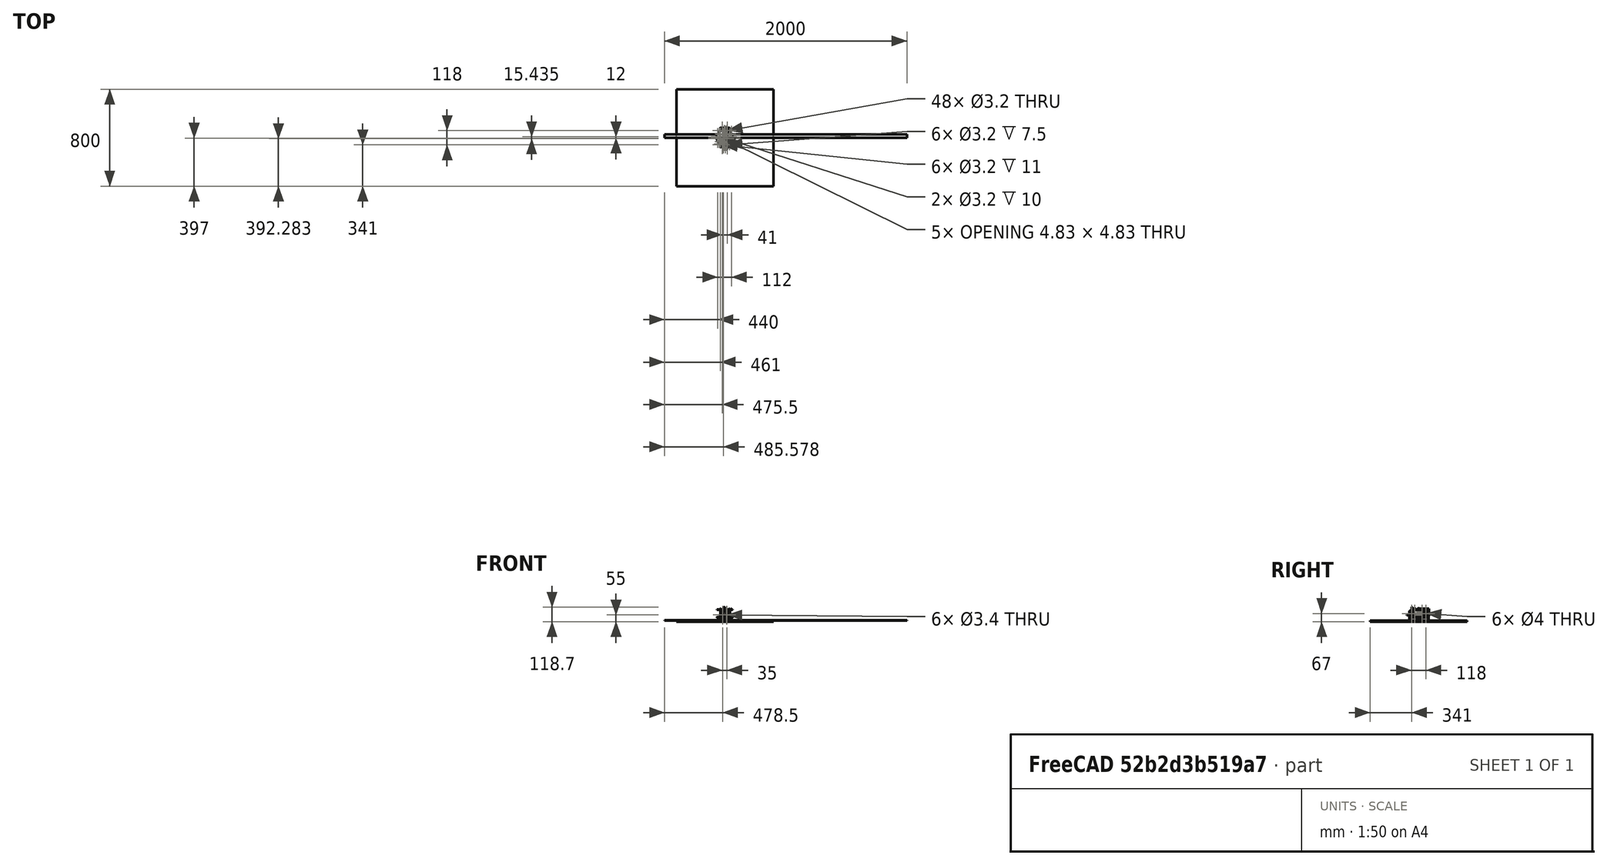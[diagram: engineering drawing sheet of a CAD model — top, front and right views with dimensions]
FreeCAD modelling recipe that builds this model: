
FCSTD DOCUMENT  (FreeCAD 0.21R33771 (Git))
Label: montajeGeneral
License: All rights reserved
LicenseURL: https://en.wikipedia.org/wiki/All_rights_reserved
objects: Part::Feature×64, Part::Cylinder×58, Part::MultiFuse×29, Mesh::Feature×11, Part::FeaturePython×10, Part::Cut×10, Part::Box×9, App::Part×7, Part::Sphere×2, Part::Torus×2
note: 184 computed .brp shape members not serialized (recipe doc carries the construction recipe); baked Part::Feature solids carry a one-line shape summary decoded from their .brp

FEATURE [Part::Cylinder] Cylinder021  label="Cilindro021"
  Angle = 360
  AttacherType = Attacher::AttachEngine3D
  FirstAngle = 0
  Height = 10
  Placement = pos=(32,-6,-20) rot=(0,0,1;0rad)
  Radius = 1.6
  SecondAngle = 0
FEATURE [Part::Cylinder] Cylinder022  label="Cilindro022"
  Angle = 360
  AttacherType = Attacher::AttachEngine3D
  FirstAngle = 0
  Height = 10
  Placement = pos=(32,5,-20) rot=(0,0,1;0rad)
  Radius = 1.6
  SecondAngle = 0
FEATURE [Part::Cylinder] Cylinder023  label="Cilindro023"
  Angle = 360
  AttacherType = Attacher::AttachEngine3D
  FirstAngle = 0
  Height = 10
  Placement = pos=(21,-6,-20) rot=(0,0,1;0rad)
  Radius = 1.6
  SecondAngle = 0
FEATURE [Part::Cylinder] Cylinder024  label="Cilindro024"
  Angle = 360
  AttacherType = Attacher::AttachEngine3D
  FirstAngle = 0
  Height = 10
  Placement = pos=(21,5,-20) rot=(0,0,1;0rad)
  Radius = 1.6
  SecondAngle = 0
FEATURE [Part::Cylinder] Cylinder025  label="Cilindro025"
  Angle = 360
  AttacherType = Attacher::AttachEngine3D
  FirstAngle = 0
  Height = 10
  Placement = pos=(32,-6,-20) rot=(0,0,1;0rad)
  Radius = 1.6
  SecondAngle = 0
FEATURE [Part::Cylinder] Cylinder026  label="Cilindro026"
  Angle = 360
  AttacherType = Attacher::AttachEngine3D
  FirstAngle = 0
  Height = 10
  Placement = pos=(32,5,-20) rot=(0,0,1;0rad)
  Radius = 1.6
  SecondAngle = 0
FEATURE [Part::Cylinder] Cylinder027  label="Cilindro027"
  Angle = 360
  AttacherType = Attacher::AttachEngine3D
  FirstAngle = 0
  Height = 10
  Placement = pos=(21,-6,-20) rot=(0,0,1;0rad)
  Radius = 1.6
  SecondAngle = 0
FEATURE [Part::Cylinder] Cylinder028  label="Cilindro028"
  Angle = 360
  AttacherType = Attacher::AttachEngine3D
  FirstAngle = 0
  Height = 10
  Placement = pos=(21,5,-20) rot=(0,0,1;0rad)
  Radius = 1.6
  SecondAngle = 0
FEATURE [Part::Cylinder] Cylinder056  label="Cilindro056"
  Angle = 360
  AttacherType = Attacher::AttachEngine3D
  FirstAngle = 0
  Height = 10
  Placement = pos=(-6,-32,-19) rot=(0,0,1;0rad)
  Radius = 1.6
  SecondAngle = 0
FEATURE [Part::Cylinder] Cylinder057  label="Cilindro057"
  Angle = 360
  AttacherType = Attacher::AttachEngine3D
  FirstAngle = 0
  Height = 10
  Placement = pos=(-6,32,-19) rot=(0,0,1;0rad)
  Radius = 1.6
  SecondAngle = 0
FEATURE [Part::Cylinder] Cylinder063  label="Cilindro063"
  Angle = 360
  AttacherType = Attacher::AttachEngine3D
  FirstAngle = 0
  Height = 50
  Placement = pos=(16.5,-58,-17) rot=(0,0,1;0rad)
  Radius = 1.6
  SecondAngle = 0
FEATURE [Part::Cylinder] Cylinder072  label="Cilindro072"
  Angle = 360
  AttacherType = Attacher::AttachEngine3D
  FirstAngle = 0
  Height = 50
  Placement = pos=(16.5,57,-17) rot=(0,0,1;0rad)
  Radius = 1.6
  SecondAngle = 0
FEATURE [Part::Cylinder] Cylinder073  label="Cilindro073"
  Angle = 360
  AttacherType = Attacher::AttachEngine3D
  FirstAngle = 0
  Height = 50
  Placement = pos=(-24.5,59,-17) rot=(0,0,1;0rad)
  Radius = 1.6
  SecondAngle = 0
FEATURE [Part::Cylinder] Cylinder074  label="Cilindro074"
  Angle = 360
  AttacherType = Attacher::AttachEngine3D
  FirstAngle = 0
  Height = 50
  Placement = pos=(-24.5,-56,-17) rot=(0,0,1;0rad)
  Radius = 1.6
  SecondAngle = 0
FEATURE [Part::MultiFuse] Fusion016
  Placement = pos=(20,0,0) rot=(0,0,1;0rad)
  Shapes = -> [Cylinder021,Cylinder022,Cylinder023,Cylinder024]
FEATURE [Part::MultiFuse] Fusion017
  Placement = pos=(-81,0,0) rot=(0,0,1;0rad)
  Shapes = -> [Cylinder025,Cylinder026,Cylinder027,Cylinder028]
FEATURE [Part::MultiFuse] Fusion018
  Shapes = -> [Fusion016,Fusion017]
FEATURE [Part::MultiFuse] Fusion034  label="taladrosAbajo"
  Shapes = -> [Cylinder063,Cylinder072,Cylinder073,Cylinder074]
FEATURE [Part::FeaturePython] Nut  label="M3-Tuerca"  # Fasteners workbench fastener (typed FeaturePython)
  Placement = pos=(-6,-32,-12) rot=(0,0,1;0rad)
  diameter = 4
  invert = false
  leftHanded = false
  matchOuter = false
  offset = 0
  thread = false
  type = 22
FEATURE [Part::FeaturePython] Nut008  label="M3-Tuerca008"  # Fasteners workbench fastener (typed FeaturePython)
  Placement = pos=(32,5,-12) rot=(0,0,1;0rad)
  diameter = 4
  invert = false
  leftHanded = false
  matchOuter = false
  offset = 0
  thread = false
  type = 24
FEATURE [Part::FeaturePython] Nut009  label="M3-Tuerca009"  # Fasteners workbench fastener (typed FeaturePython)
  Placement = pos=(21,5,-12) rot=(0,0,1;0rad)
  diameter = 4
  invert = false
  leftHanded = false
  matchOuter = false
  offset = 0
  thread = false
  type = 24
FEATURE [Part::FeaturePython] Nut010  label="M3-Tuerca010"  # Fasteners workbench fastener (typed FeaturePython)
  Placement = pos=(32,-6,-12) rot=(0,0,1;0rad)
  diameter = 4
  invert = false
  leftHanded = false
  matchOuter = false
  offset = 0
  thread = false
  type = 24
FEATURE [Part::FeaturePython] Nut011  label="M3-Tuerca011"  # Fasteners workbench fastener (typed FeaturePython)
  Placement = pos=(21,-6,-12) rot=(0,0,1;0rad)
  diameter = 4
  invert = false
  leftHanded = false
  matchOuter = false
  offset = 0
  thread = false
  type = 24
FEATURE [Part::MultiFuse] Fusion007
  Placement = pos=(20,0,0) rot=(0,0,1;0rad)
  Shapes = -> [Nut011,Nut010,Nut009,Nut008]
FEATURE [Part::FeaturePython] Nut012  label="M3-Tuerca012"  # Fasteners workbench fastener (typed FeaturePython)
  Placement = pos=(32,5,-12) rot=(0,0,1;0rad)
  diameter = 4
  invert = false
  leftHanded = false
  matchOuter = false
  offset = 0
  thread = false
  type = 24
FEATURE [Part::FeaturePython] Nut013  label="M3-Tuerca013"  # Fasteners workbench fastener (typed FeaturePython)
  Placement = pos=(21,5,-12) rot=(0,0,1;0rad)
  diameter = 4
  invert = false
  leftHanded = false
  matchOuter = false
  offset = 0
  thread = false
  type = 24
FEATURE [Part::FeaturePython] Nut014  label="M3-Tuerca014"  # Fasteners workbench fastener (typed FeaturePython)
  Placement = pos=(32,-6,-12) rot=(0,0,1;0rad)
  diameter = 4
  invert = false
  leftHanded = false
  matchOuter = false
  offset = 0
  thread = false
  type = 24
FEATURE [Part::FeaturePython] Nut015  label="M3-Tuerca015"  # Fasteners workbench fastener (typed FeaturePython)
  Placement = pos=(21,-6,-12) rot=(0,0,1;0rad)
  diameter = 4
  invert = false
  leftHanded = false
  matchOuter = false
  offset = 0
  thread = false
  type = 24
FEATURE [Part::MultiFuse] Fusion008
  Placement = pos=(-81,0,0) rot=(0,0,1;0rad)
  Shapes = -> [Nut015,Nut014,Nut013,Nut012]
FEATURE [Part::MultiFuse] Fusion009
  Shapes = -> [Fusion008,Fusion007]
FEATURE [Part::FeaturePython] Nut016  label="M3-Tuerca016"  # Fasteners workbench fastener (typed FeaturePython)
  Placement = pos=(-6,32,-12) rot=(0,0,1;0rad)
  diameter = 4
  invert = false
  leftHanded = false
  matchOuter = false
  offset = 0
  thread = false
  type = 22
FEATURE [Part::MultiFuse] Fusion
  Shapes = -> [Nut016,Nut,Cylinder057,Cylinder056]
FEATURE [Part::MultiFuse] Fusion033
  Shapes = -> [Fusion,Fusion018,Fusion009]
FEATURE [Part::MultiFuse] Fusion036
  Shapes = -> [Fusion033,Fusion034]
FEATURE [Part::Cylinder] Cylinder  label="Cilindro"
  Angle = 360
  AttacherType = Attacher::AttachEngine3D
  FirstAngle = 0
  Height = 150
  Placement = pos=(13.5,50,7) rot=(1,0,0;1.5708rad)
  Radius = 1.7
  SecondAngle = 0
FEATURE [Part::Cylinder] Cylinder009  label="Cilindro009"
  Angle = 360
  AttacherType = Attacher::AttachEngine3D
  FirstAngle = 0
  Height = 150
  Placement = pos=(-21.5,50,7) rot=(1,0,0;1.5708rad)
  Radius = 1.7
  SecondAngle = 0
FEATURE [Part::Cylinder] Cylinder061  label="Cilindro061"
  Angle = 360
  AttacherType = Attacher::AttachEngine3D
  FirstAngle = 0
  Height = 150
  Placement = pos=(13.5,50,7) rot=(1,0,0;1.5708rad)
  Radius = 1.7
  SecondAngle = 0
FEATURE [Part::MultiFuse] Fusion002
  Placement = pos=(-8,-24.99,0) rot=(0,0,1;3.14159rad)
  Shapes = -> [Cylinder,Cylinder009]
FEATURE [Mesh::Feature] _8BYJ_48_v007  label="28BYJ-48_v007"
  Placement = pos=(-8.5,-32.05,4.5) rot=(0,0,1;3.14159rad)
FEATURE [Mesh::Feature] _8BYJ_48_v6  label="28BYJ-48_v6"
  Placement = pos=(0.5,33,5) rot=(0,0,1;0rad)
FEATURE [Part::Box] Box001  label="Cubo001"
  AttacherType = Attacher::AttachEngine3D
  Height = 60
  Length = 20
  Width = 80
FEATURE [Part::Cylinder] Cylinder075  label="Cilindro075"
  Angle = 360
  AttacherType = Attacher::AttachEngine3D
  FirstAngle = 0
  Height = 50
  Placement = pos=(-8,8,30) rot=(0,1,0;1.5708rad)
  Radius = 1.5
  SecondAngle = 0
FEATURE [Part::Cylinder] Cylinder076  label="Cilindro076"
  Angle = 360
  AttacherType = Attacher::AttachEngine3D
  FirstAngle = 0
  Height = 50
  Placement = pos=(-8,72,30) rot=(0,1,0;1.5708rad)
  Radius = 1.5
  SecondAngle = 0
FEATURE [Part::MultiFuse] Fusion037
  Shapes = -> [Cylinder076,Cylinder075]
FEATURE [Part::Cut] Cut001  label="portaPilasx5"
  Base = -> Box001
  Placement = pos=(19,-40,-11) rot=(0,0,1;0rad)
  Tool = -> Fusion037
FEATURE [Part::Box] Box002  label="Cubo002"
  AttacherType = Attacher::AttachEngine3D
  Height = 60
  Length = 20
  Width = 80
FEATURE [Part::Cylinder] Cylinder077  label="Cilindro077"
  Angle = 360
  AttacherType = Attacher::AttachEngine3D
  FirstAngle = 0
  Height = 50
  Placement = pos=(-8,8,30) rot=(0,1,0;1.5708rad)
  Radius = 1.5
  SecondAngle = 0
FEATURE [Part::Cylinder] Cylinder078  label="Cilindro078"
  Angle = 360
  AttacherType = Attacher::AttachEngine3D
  FirstAngle = 0
  Height = 50
  Placement = pos=(-8,72,30) rot=(0,1,0;1.5708rad)
  Radius = 1.5
  SecondAngle = 0
FEATURE [Part::MultiFuse] Fusion038
  Shapes = -> [Cylinder078,Cylinder077]
FEATURE [Part::Cut] Cut002  label="portaPilasx006"
  Base = -> Box002
  Placement = pos=(-1,5,0) rot=(0,0,1;0rad)
  Tool = -> Fusion038
FEATURE [Part::Feature] Cut_solid002  label="columna (Solid)"
  Placement = pos=(-1,5,0) rot=(0,0,1;0rad)
  shape: bbox 10 x 10 x 60 mm, 24 faces (baked)
FEATURE [Part::Feature] Cut_solid003  label="columna (Solid)001"
  Placement = pos=(-1,67,0) rot=(0,0,1;0rad)
  shape: bbox 10 x 10 x 60 mm, 24 faces (baked)
FEATURE [Part::Feature] Cut_solid004  label="columna (Solid)002"
  Placement = pos=(-8,21,0) rot=(0,0,1;3.14159rad)
  shape: bbox 10 x 10 x 60 mm, 24 faces (baked)
FEATURE [Part::Feature] Cut_solid005  label="columna (Solid)003"
  Placement = pos=(0,97,0) rot=(0,0,1;0rad)
  shape: bbox 10 x 10 x 60 mm, 24 faces (baked)
FEATURE [Part::Feature] Cut_solid006  label="columna (Solid)004"
  Placement = pos=(0,-21,0) rot=(0,0,1;0rad)
  shape: bbox 10 x 10 x 60 mm, 24 faces (baked)
FEATURE [Part::Feature] Cut_solid007  label="columna (Solid)005"
  Placement = pos=(-8,-96,0) rot=(0,0,1;3.14159rad)
  shape: bbox 10 x 10 x 60 mm, 24 faces (baked)
FEATURE [Part::Cylinder] Cylinder104  label="Cilindro104"
  Angle = 360
  AttacherType = Attacher::AttachEngine3D
  FirstAngle = 0
  Height = 20
  Placement = pos=(-6,0,43) rot=(0,0,1;0rad)
  Radius = 5
  SecondAngle = 0
FEATURE [Mesh::Feature] Arduino_ipt  label="Arduino.ipt"
  Placement = pos=(-8,15,90) rot=(0,0,1;3.14159rad)
FEATURE [Part::Box] Box027  label="Cubo027"
  AttacherType = Attacher::AttachEngine3D
  Height = 7
  Length = 7.5
  Placement = pos=(-25,-9,46) rot=(0,0,1;0rad)
  Width = 16
FEATURE [Mesh::Feature] rueda_ojo
  Placement = pos=(-2,83,33) rot=(1,0,0;1.5708rad)
FEATURE [Mesh::Feature] rueda_ojo001
  Placement = pos=(-2,-80,-34.5) rot=(1,0,0;-1.5708rad)
FEATURE [Part::Box] Box  label="suelo"
  AttacherType = Attacher::AttachEngine3D
  Height = 10
  Length = 800
  Placement = pos=(-400,-400,-48) rot=(0,0,1;0rad)
  Width = 800
FEATURE [Part::Box] Box008  label="Cubo008"
  AttacherType = Attacher::AttachEngine3D
  Height = 3
  Length = 15
  Placement = pos=(-8,-8,4) rot=(0,0,1;0rad)
  Width = 15
FEATURE [Part::Cylinder] Cylinder011  label="Cilindro011"
  Angle = 360
  AttacherType = Attacher::AttachEngine3D
  FirstAngle = 0
  Height = 15
  Placement = pos=(0,0,-15) rot=(0,0,1;0rad)
  Radius = 4
  SecondAngle = 0
FEATURE [Part::Cylinder] Cylinder012  label="Cilindro012"
  Angle = 360
  AttacherType = Attacher::AttachEngine3D
  FirstAngle = 0
  Height = 10
  Placement = pos=(32,-6,-20) rot=(0,0,1;0rad)
  Radius = 1.6
  SecondAngle = 0
FEATURE [Part::Cylinder] Cylinder013  label="Cilindro013"
  Angle = 360
  AttacherType = Attacher::AttachEngine3D
  FirstAngle = 0
  Height = 10
  Placement = pos=(32,5,-20) rot=(0,0,1;0rad)
  Radius = 1.6
  SecondAngle = 0
FEATURE [Part::Cylinder] Cylinder014  label="Cilindro014"
  Angle = 360
  AttacherType = Attacher::AttachEngine3D
  FirstAngle = 0
  Height = 10
  Placement = pos=(21,-6,-20) rot=(0,0,1;0rad)
  Radius = 1.6
  SecondAngle = 0
FEATURE [Part::Cylinder] Cylinder015  label="Cilindro015"
  Angle = 360
  AttacherType = Attacher::AttachEngine3D
  FirstAngle = 0
  Height = 10
  Placement = pos=(21,5,-20) rot=(0,0,1;0rad)
  Radius = 1.6
  SecondAngle = 0
FEATURE [Part::MultiFuse] Fusion005
  Shapes = -> [Cylinder012,Cylinder013,Cylinder014,Cylinder015]
FEATURE [Part::Sphere] Sphere  label="Esfera"
  Angle1 = -90
  Angle2 = 90
  Angle3 = 360
  AttacherType = Attacher::AttachEngine3D
  Placement = pos=(0,0,-16) rot=(0,0,1;0rad)
  Radius = 4
FEATURE [Part::MultiFuse] Fusion010
  Placement = pos=(0,0,4) rot=(0,0,1;0rad)
  Shapes = -> [Cylinder011,Sphere]
FEATURE [Part::MultiFuse] Fusion011  label="ballcaster"
  Placement = pos=(27,0,-22) rot=(0,0,1;0rad)
  Shapes = -> [Fusion010,Box008]
FEATURE [Part::Cut] Cut009  label="ballCasterA"
  Base = -> Fusion011
  Placement = pos=(20,0,0) rot=(0,0,1;0rad)
  Tool = -> Fusion005
FEATURE [Part::Box] Box028  label="portapilasx6"
  AttacherType = Attacher::AttachEngine3D
  Height = 60
  Length = 45
  Placement = pos=(-38,-42,-10) rot=(0,0,1;0rad)
  Width = 30
FEATURE [Part::Feature] Fusion060_solid  label="plataformaInferior (Solid)"
  shape: bbox 130 x 130 x 13 mm, 195 faces (baked)
FEATURE [Mesh::Feature] HC_SR04
  Placement = pos=(90,0,3) rot=(0.57735,-0.57735,0.57735;4.18879rad)
FEATURE [Mesh::Feature] Mesh  label="soporteSensores001"
  Placement = pos=(17,0,0) rot=(0,0,1;0rad)
FEATURE [Part::Box] Box029  label="Cubo028"
  AttacherType = Attacher::AttachEngine3D
  Height = 3
  Length = 15
  Placement = pos=(-8,-8,4) rot=(0,0,1;0rad)
  Width = 15
FEATURE [Part::Cylinder] Cylinder113  label="Cilindro113"
  Angle = 360
  AttacherType = Attacher::AttachEngine3D
  FirstAngle = 0
  Height = 15
  Placement = pos=(0,0,-15) rot=(0,0,1;0rad)
  Radius = 4
  SecondAngle = 0
FEATURE [Part::Cylinder] Cylinder114  label="Cilindro114"
  Angle = 360
  AttacherType = Attacher::AttachEngine3D
  FirstAngle = 0
  Height = 10
  Placement = pos=(32,-6,-20) rot=(0,0,1;0rad)
  Radius = 1.6
  SecondAngle = 0
FEATURE [Part::Cylinder] Cylinder115  label="Cilindro115"
  Angle = 360
  AttacherType = Attacher::AttachEngine3D
  FirstAngle = 0
  Height = 10
  Placement = pos=(32,5,-20) rot=(0,0,1;0rad)
  Radius = 1.6
  SecondAngle = 0
FEATURE [Part::Cylinder] Cylinder116  label="Cilindro116"
  Angle = 360
  AttacherType = Attacher::AttachEngine3D
  FirstAngle = 0
  Height = 10
  Placement = pos=(21,-6,-20) rot=(0,0,1;0rad)
  Radius = 1.6
  SecondAngle = 0
FEATURE [Part::Cylinder] Cylinder117  label="Cilindro117"
  Angle = 360
  AttacherType = Attacher::AttachEngine3D
  FirstAngle = 0
  Height = 10
  Placement = pos=(21,5,-20) rot=(0,0,1;0rad)
  Radius = 1.6
  SecondAngle = 0
FEATURE [Part::MultiFuse] Fusion058
  Shapes = -> [Cylinder114,Cylinder115,Cylinder116,Cylinder117]
FEATURE [Part::Sphere] Sphere001  label="Esfera001"
  Angle1 = -90
  Angle2 = 90
  Angle3 = 360
  AttacherType = Attacher::AttachEngine3D
  Placement = pos=(0,0,-16) rot=(0,0,1;0rad)
  Radius = 4
FEATURE [Part::MultiFuse] Fusion059
  Placement = pos=(0,0,4) rot=(0,0,1;0rad)
  Shapes = -> [Cylinder113,Sphere001]
FEATURE [Part::MultiFuse] Fusion060  label="ballcaster001"
  Placement = pos=(27,0,-22) rot=(0,0,1;0rad)
  Shapes = -> [Fusion059,Box029]
FEATURE [Part::Cut] Cut019  label="ballCasterA001"
  Base = -> Fusion060
  Placement = pos=(-81,0.5,0) rot=(0,0,1;0rad)
  Tool = -> Fusion058
FEATURE [Mesh::Feature] Arduino_ipt001  label="Arduino.ipt001"
  Placement = pos=(-8,15,93) rot=(0,0,1;3.14159rad)
FEATURE [Part::Box] Box030  label="Cubo029"
  AttacherType = Attacher::AttachEngine3D
  Height = 7
  Length = 7.5
  Placement = pos=(-25,-9,46) rot=(0,0,1;0rad)
  Width = 16
FEATURE [Part::Cylinder] Cylinder118  label="Cilindro118"
  Angle = 360
  AttacherType = Attacher::AttachEngine3D
  FirstAngle = 0
  Height = 10
  Placement = pos=(-15,-50,45) rot=(0,0,1;0rad)
  Radius = 1.6
  SecondAngle = 0
FEATURE [Part::Cylinder] Cylinder034  label="Cilindro034"
  Angle = 360
  AttacherType = Attacher::AttachEngine3D
  FirstAngle = 0
  Height = 10
  Placement = pos=(-27,-22,24) rot=(0,0,1;0rad)
  Radius = 1.6
  SecondAngle = 0
FEATURE [Part::Cylinder] Cylinder035  label="Cilindro035"
  Angle = 360
  AttacherType = Attacher::AttachEngine3D
  FirstAngle = 0
  Height = 10
  Placement = pos=(24,11,24) rot=(0,0,1;0rad)
  Radius = 1.6
  SecondAngle = 0
FEATURE [Part::Cylinder] Cylinder036  label="Cilindro036"
  Angle = 360
  AttacherType = Attacher::AttachEngine3D
  FirstAngle = 0
  Height = 10
  Placement = pos=(24,-17,24) rot=(0,0,1;0rad)
  Radius = 1.6
  SecondAngle = 0
FEATURE [Part::Cylinder] Cylinder037  label="Cilindro037"
  Angle = 360
  AttacherType = Attacher::AttachEngine3D
  FirstAngle = 0
  Height = 10
  Placement = pos=(-26,26.5,24) rot=(0,0,1;0rad)
  Radius = 1.6
  SecondAngle = 0
FEATURE [Part::Cylinder] Cylinder038  label="Cilindro038"
  Angle = 360
  AttacherType = Attacher::AttachEngine3D
  FirstAngle = 0
  Height = 6
  Placement = pos=(-27,-22,28) rot=(0,0,1;0rad)
  Radius = 2.5
  SecondAngle = 0
FEATURE [Part::Cylinder] Cylinder039  label="Cilindro039"
  Angle = 360
  AttacherType = Attacher::AttachEngine3D
  FirstAngle = 0
  Height = 6
  Placement = pos=(24,11,28) rot=(0,0,1;0rad)
  Radius = 2.5
  SecondAngle = 0
FEATURE [Part::Cylinder] Cylinder040  label="Cilindro040"
  Angle = 360
  AttacherType = Attacher::AttachEngine3D
  FirstAngle = 0
  Height = 6
  Placement = pos=(24,-17,28) rot=(0,0,1;0rad)
  Radius = 2.5
  SecondAngle = 0
FEATURE [Part::Cylinder] Cylinder041  label="Cilindro041"
  Angle = 360
  AttacherType = Attacher::AttachEngine3D
  FirstAngle = 0
  Height = 6
  Placement = pos=(-26,26.5,28) rot=(0,0,1;0rad)
  Radius = 2.5
  SecondAngle = 0
FEATURE [Part::Cylinder] Cylinder042  label="Cilindro042"
  Angle = 360
  AttacherType = Attacher::AttachEngine3D
  FirstAngle = 0
  Height = 6
  Placement = pos=(35,9,28) rot=(0,0,1;0rad)
  Radius = 2.5
  SecondAngle = 0
FEATURE [Part::Cylinder] Cylinder044  label="Cilindro044"
  Angle = 360
  AttacherType = Attacher::AttachEngine3D
  FirstAngle = 0
  Height = 6
  Placement = pos=(35,-3,28) rot=(0,0,1;0rad)
  Radius = 2.5
  SecondAngle = 0
FEATURE [Part::Cylinder] Cylinder099  label="Cilindro099"
  Angle = 360
  AttacherType = Attacher::AttachEngine3D
  FirstAngle = 0
  Height = 4
  Placement = pos=(-4,0,49) rot=(0,0,1;0rad)
  Radius = 65
  SecondAngle = 0
FEATURE [Part::Cylinder] Cylinder100  label="Cilindro100"
  Angle = 360
  AttacherType = Attacher::AttachEngine3D
  FirstAngle = 0
  Height = 50
  Placement = pos=(16.5,-58.8,-17) rot=(0,0,1;0rad)
  Radius = 1.6
  SecondAngle = 0
FEATURE [Part::Cylinder] Cylinder101  label="Cilindro101"
  Angle = 360
  AttacherType = Attacher::AttachEngine3D
  FirstAngle = 0
  Height = 50
  Placement = pos=(16.5,59,-17) rot=(0,0,1;0rad)
  Radius = 1.6
  SecondAngle = 0
FEATURE [Part::Cylinder] Cylinder102  label="Cilindro102"
  Angle = 360
  AttacherType = Attacher::AttachEngine3D
  FirstAngle = 0
  Height = 50
  Placement = pos=(-24.5,59,-17) rot=(0,0,1;0rad)
  Radius = 1.6
  SecondAngle = 0
FEATURE [Part::Cylinder] Cylinder103  label="Cilindro103"
  Angle = 360
  AttacherType = Attacher::AttachEngine3D
  FirstAngle = 0
  Height = 50
  Placement = pos=(-24.5,-58,-17) rot=(0,0,1;0rad)
  Radius = 1.6
  SecondAngle = 0
FEATURE [Part::Cylinder] Cylinder119  label="Cilindro119"
  Angle = 360
  AttacherType = Attacher::AttachEngine3D
  FirstAngle = 0
  Height = 20
  Placement = pos=(-6,0,43) rot=(0,0,1;0rad)
  Radius = 5
  SecondAngle = 0
FEATURE [Part::Cylinder] Cylinder105  label="Cilindro105"
  Angle = 360
  AttacherType = Attacher::AttachEngine3D
  FirstAngle = 0
  Height = 50
  Placement = pos=(36,-24,43) rot=(0,0,1;0rad)
  Radius = 1.6
  SecondAngle = 0
FEATURE [Part::Cylinder] Cylinder106  label="Cilindro106"
  Angle = 360
  AttacherType = Attacher::AttachEngine3D
  FirstAngle = 0
  Height = 50
  Placement = pos=(8,-24,43) rot=(0,0,1;0rad)
  Radius = 1.6
  SecondAngle = 0
FEATURE [Part::Cylinder] Cylinder107  label="Cilindro107"
  Angle = 360
  AttacherType = Attacher::AttachEngine3D
  FirstAngle = 0
  Height = 50
  Placement = pos=(51.5,26,43) rot=(0,0,1;0rad)
  Radius = 1.6
  SecondAngle = 0
FEATURE [Part::Cylinder] Cylinder108  label="Cilindro108"
  Angle = 360
  AttacherType = Attacher::AttachEngine3D
  FirstAngle = 0
  Height = 50
  Placement = pos=(3,27,43) rot=(0,0,1;0rad)
  Radius = 1.6
  SecondAngle = 0
FEATURE [Part::Cylinder] Cylinder109  label="Cilindro109"
  Angle = 360
  AttacherType = Attacher::AttachEngine3D
  FirstAngle = 0
  Height = 50
  Placement = pos=(15.5,-33,19) rot=(0,0,1;0rad)
  Radius = 1.6
  SecondAngle = 0
FEATURE [Part::Cylinder] Cylinder110  label="Cilindro110"
  Angle = 360
  AttacherType = Attacher::AttachEngine3D
  FirstAngle = 0
  Height = 50
  Placement = pos=(15.5,29,19) rot=(0,0,1;0rad)
  Radius = 1.6
  SecondAngle = 0
FEATURE [Part::Cylinder] Cylinder120  label="Cilindro120"
  Angle = 360
  AttacherType = Attacher::AttachEngine3D
  FirstAngle = 0
  Height = 20
  Placement = pos=(-39,-3,47) rot=(0,0,1;0rad)
  Radius = 1.6
  SecondAngle = 0
FEATURE [Part::Cylinder] Cylinder121  label="Cilindro121"
  Angle = 360
  AttacherType = Attacher::AttachEngine3D
  FirstAngle = 0
  Height = 20
  Placement = pos=(-39,9,47) rot=(0,0,1;0rad)
  Radius = 1.6
  SecondAngle = 0
FEATURE [Part::Cylinder] Cylinder122  label="Cilindro122"
  Angle = 360
  AttacherType = Attacher::AttachEngine3D
  FirstAngle = 0
  Height = 10
  Placement = pos=(1,-50,45) rot=(0,0,1;0rad)
  Radius = 1.6
  SecondAngle = 0
FEATURE [Part::MultiFuse] Fusion061
  Shapes = -> [Cylinder122,Cylinder118]
FEATURE [Part::MultiFuse] Fusion021
  Shapes = -> [Cylinder038,Cylinder039,Cylinder040,Cylinder041]
FEATURE [Part::MultiFuse] Fusion022
  Shapes = -> [Cylinder034,Cylinder035,Cylinder036,Cylinder037]
FEATURE [Part::Cut] Cut014
  Base = -> Fusion021
  Placement = pos=(25,0,24) rot=(0,0,-1;1.5708rad)
  Tool = -> Fusion022
FEATURE [Part::MultiFuse] Fusion028
  Placement = pos=(-74,0,25) rot=(0,0,1;0rad)
  Shapes = -> [Cylinder044,Cylinder042]
FEATURE [Part::MultiFuse] Fusion052  label="taladrosArriba"
  Placement = pos=(0,0,49) rot=(0,0,1;0rad)
  Shapes = -> [Cylinder100,Cylinder101,Cylinder102,Cylinder103]
FEATURE [Part::Cut] Cut015
  Base = -> Cylinder099
  Tool = -> Fusion052
FEATURE [Part::MultiFuse] Fusion053
  Shapes = -> [Cut015,Cut014]
FEATURE [Part::MultiFuse] Fusion054
  Shapes = -> [Cylinder105,Cylinder106,Cylinder107,Cylinder108]
FEATURE [Part::Cut] Cut016
  Base = -> Fusion053
  Tool = -> Fusion054
FEATURE [Part::MultiFuse] Fusion055
  Shapes = -> [Cylinder110,Cylinder109]
FEATURE [Part::Cut] Cut017
  Base = -> Cut016
  Tool = -> Fusion055
FEATURE [Part::MultiFuse] Fusion062
  Shapes = -> [Box030,Cylinder119,Cylinder120,Cylinder121]
FEATURE [Part::MultiFuse] Fusion057
  Shapes = -> [Cut017,Fusion028]
FEATURE [Part::Cut] Cut018  label="plataformaS"
  Base = -> Fusion057
  Tool = -> Fusion062
FEATURE [Part::Cut] Cut  label="plataformaSuperior"
  Base = -> Cut018
  Tool = -> Fusion061
FEATURE [Mesh::Feature] ULN2003_Stepper_Driver
  Placement = pos=(-51.5,-18.5,61) rot=(0,0,1;0rad)
FEATURE [Mesh::Feature] ULN2003_Stepper_Driver001
  Placement = pos=(-51.5,24.5,61) rot=(0,0,1;0rad)
FEATURE [Part::Feature] Cut_solid  label="plataformaSuperior (Solid)"
  shape: bbox 130 x 130 x 10 mm, 42 faces (baked)
FEATURE [Part::Feature] Part_solid  label="soporte-zumbador-src (Solid)"
  Placement = pos=(-7,-58.5,63) rot=(0,0,1;1.5708rad)
  shape: bbox 23.6 x 12.17 x 17.7 mm, 18 faces (baked)
FEATURE [Part::Feature] Part__Feature  label="CELECPORTABATERIAS._MAQUINADA.stp_Predeterminado"
  shape: bbox 46.99 x 29.69 x 58.8 mm, 1017 faces (baked)
FEATURE [Part::Feature] Part__Feature001  label="CELECTAPA PORTA BATERIAS_MAQUINADA.stp_Predeterminado"
  Placement = pos=(0,0,-29.7005) rot=(1,0,0;1.5708rad)
  shape: bbox 45 x 28 x 0.762 mm, 10 faces (baked)
FEATURE [Part::Feature] Part__Feature002  label="CELECTAPA PORTA BATERIAS_Superior_MAQUINADA.stp_Predeterminado"
  Placement = pos=(-3e-15,0,29.7005) rot=(-1,0,0;1.5708rad)
  shape: bbox 45 x 28 x 0.762 mm, 15 faces (baked)
FEATURE [Part::Feature] Part__Feature003  label="CELECESPIRAL_CON ESTRELLA.stp_Predeterminado"
  Placement = pos=(15.4548,-6.67262,-24.1599) rot=(0,0,-1;1.49913rad)
  shape: bbox 16.91 x 22.54 x 12.64 mm, 61 faces (baked)
FEATURE [Part::Feature] Part__Feature004  label="CELECESPIRAL_CON ESTRELLA.stp_Predeterminado001"
  Placement = pos=(-14.4254,-7.48783,-24.1599) rot=(0,0,1;3.12567rad)
  shape: bbox 22.08 x 16.49 x 12.64 mm, 61 faces (baked)
FEATURE [Part::Feature] Part__Feature005  label="CELECESPIRAL_CON ESTRELLA.stp_Predeterminado002"
  Placement = pos=(-0.00369639,7.20602,-24.1599) rot=(0,0,-1;0.035464rad)
  shape: bbox 22.25 x 16.65 x 12.64 mm, 61 faces (baked)
FEATURE [Part::Feature] Part__Feature006  label="CELECESPIRAL_CON ESTRELLA.stp_Predeterminado003"
  Placement = pos=(-14.6786,6.70736,24.1599) rot=(0.700786,0.713371,0;3.14159rad)
  shape: bbox 16.51 x 22.1 x 12.64 mm, 61 faces (baked)
FEATURE [Part::Feature] Part__Feature007  label="CELECESPIRAL_CON ESTRELLA.stp_Predeterminado004"
  Placement = pos=(14.4272,7.71755,24.1599) rot=(1,0,0;3.14159rad)
  shape: bbox 21.96 x 16.37 x 12.64 mm, 61 faces (baked)
FEATURE [Part::Feature] Part__Feature008  label="CELECESTRELLA_A.stp_Predeterminado"
  Placement = pos=(28.849,-7.71755,24.1599) rot=(1,0,0;3.14159rad)
  shape: bbox 6.876 x 7.622 x 2.232 mm, 46 faces (baked)
FEATURE [Part::Feature] Part__Feature009  label="CELECESPIRAL_A..stp_Predeterminado"
  Placement = pos=(0,-7.71755,24.1599) rot=(0,1,0;3.14159rad)
  shape: bbox 8.437 x 16.37 x 11.43 mm, 7 faces (baked)
FEATURE [Part::Feature] Part__Feature010  label="Pila AA_Predeterminado"
  Placement = pos=(-14.4218,-7.71755,-24.1001) rot=(-0.04052,0.706526,0.706526;3.22259rad)
  shape: bbox 14.05 x 14.05 x 50.29 mm, 15 faces (baked)
FEATURE [Part::Feature] Part__Feature011  label="Pila AA_Predeterminado001"
  Placement = pos=(5e-14,-7.71755,24.1001) rot=(-0.089608,0.704262,-0.704262;2.96285rad)
  shape: bbox 14.05 x 14.05 x 50.29 mm, 15 faces (baked)
FEATURE [Part::Feature] Part__Feature012  label="Pila AA_Predeterminado002"
  Placement = pos=(14.4218,-7.71755,-24.1001) rot=(-0.099643,0.703588,0.703588;3.34022rad)
  shape: bbox 14.05 x 14.05 x 50.29 mm, 15 faces (baked)
FEATURE [Part::Feature] Part__Feature013  label="Pila AA_Predeterminado003"
  Placement = pos=(14.4218,7.71755,24.1001) rot=(-0.184251,0.695001,-0.695001;2.77718rad)
  shape: bbox 14.05 x 14.05 x 50.29 mm, 15 faces (baked)
FEATURE [Part::Feature] Part__Feature014  label="Pila AA_Predeterminado004"
  Placement = pos=(0,7.71755,-24.1001) rot=(-0.109497,0.702855,0.702855;3.35972rad)
  shape: bbox 14.05 x 14.05 x 50.29 mm, 15 faces (baked)
FEATURE [Part::Feature] Part__Feature015  label="Pila AA_Predeterminado005"
  Placement = pos=(-14.4218,7.71755,24.1001) rot=(-0.261873,0.68243,-0.68243;2.62935rad)
  shape: bbox 14.05 x 14.05 x 50.29 mm, 15 faces (baked)
FEATURE [App::Part] Portabaterias_AA  label="Portabaterias AA"
  Group = -> [Part__Feature,Part__Feature001,Part__Feature002,Part__Feature003,Part__Feature004,Part__Feature005,Part__Feature006,Part__Feature007,Part__Feature008,Part__Feature009,Part__Feature010,Part__Feature011,Part__Feature012,Part__Feature013,Part__Feature014,Part__Feature015]
  Origin = -> Origin
  Placement = pos=(-15,-27,19) rot=(0,0,1;0rad)
FEATURE [Part::Feature] Part__Feature016  label="3362P-1-102LF"
  Placement = pos=(0.5,-3.2,1.53) rot=(1,0,0;1.5708rad)
  shape: bbox 6.672 x 6.672 x 7.467 mm, 233 faces, 2 solids (baked)
FEATURE [Part::Feature] Part__Feature017  label="IR_Sensor_FC-51"
  shape: bbox 31 x 14 x 1.25 mm, 435 faces (baked)
FEATURE [Part::Feature] Part__Feature018  label="KPTR-3216CGCK"
  Placement = pos=(-8.7,3.8,1.45) rot=(1,0,0;3.14159rad)
  shape: bbox 3.203 x 1.603 x 1.053 mm, 75 faces, 4 solids (baked)
FEATURE [Part::Feature] Part__Feature019  label="KPTR-3216CGCK001"
  Placement = pos=(-8.7,-3.8,1.45) rot=(1,0,0;3.14159rad)
  shape: bbox 3.203 x 1.603 x 1.053 mm, 75 faces, 4 solids (baked)
FEATURE [Part::Feature] Part__Feature020  label="COMPOUND"
  shape: bbox 5.5 x 6.7 x 11.78 mm, 50 faces, 3 solids (baked)
FEATURE [Part::Feature] Part__Feature021  label="COMPOUND001"
  shape: bbox 3.2 x 2 x 0.48 mm, 0 faces, 0 solids (baked)
FEATURE [App::Part] LED_5mm  label="LED 5mm"
  Group = -> [Part__Feature020,Part__Feature021]
  Origin = -> Origin001
  Placement = pos=(15.74,3.64,3) rot=(0.57735,0.57735,0.57735;2.0944rad)
FEATURE [Part::Feature] Part__Feature022  label="COMPOUND002"
  shape: bbox 5.5 x 6.7 x 11.78 mm, 50 faces, 3 solids (baked)
FEATURE [Part::Feature] Part__Feature023  label="COMPOUND003"
  shape: bbox 3.2 x 2 x 0.48 mm, 0 faces, 0 solids (baked)
FEATURE [App::Part] LED_5mm_foto  label="LED 5mm_foto"
  Group = -> [Part__Feature022,Part__Feature023]
  Origin = -> Origin002
  Placement = pos=(15.74,-3.64,3) rot=(0.57735,0.57735,0.57735;2.0944rad)
FEATURE [Part::Feature] Part__Feature024  label="RESC-0805"
  Placement = pos=(-4.525,-3.15,1.2) rot=(0,0,-1;1.5708rad)
  shape: bbox 1.35 x 2.1 x 0.6 mm, 52 faces, 3 solids (baked)
FEATURE [Part::Feature] Part__Feature025  label="RESC-0806"
  Placement = pos=(-4.525,3.25,1.2) rot=(0,0,1;1.5708rad)
  shape: bbox 1.35 x 2.1 x 0.6 mm, 52 faces, 3 solids (baked)
FEATURE [Part::Feature] Part__Feature026  label="SOIC8-150-50"
  Placement = pos=(0.55,3.85,1.2) rot=(1,0,0;1.5708rad)
  shape: bbox 6 x 4.9 x 1.91 mm, 105 faces (baked)
FEATURE [Part::Feature] Part__Feature027  label="1 Pin 2.54 mm Right Angle Single Row Pin Header Male 90 degrees Needl
e Connector"
  Placement = pos=(-13.5,2.54,-1.76) rot=(0,0,1;3.14159rad)
  shape: bbox 8.45 x 2.54 x 7.3 mm, 40 faces, 2 solids (baked)
FEATURE [Part::Feature] Part__Feature028  label="1 Pin 2.54 mm Right Angle Single Row Pin Header Male 90 degrees Needl
e Connector001"
  Placement = pos=(-13.5,2e-15,-1.76) rot=(0,0,1;3.14159rad)
  shape: bbox 8.45 x 2.54 x 7.3 mm, 40 faces, 2 solids (baked)
FEATURE [Part::Feature] Part__Feature029  label="1 Pin 2.54 mm Right Angle Single Row Pin Header Male 90 degrees Needl
e Connector002"
  Placement = pos=(-13.5,-2.54,-1.76) rot=(0,0,1;3.14159rad)
  shape: bbox 8.45 x 2.54 x 7.3 mm, 40 faces, 2 solids (baked)
FEATURE [Part::Feature] Part__Feature030  label="RESC-0807"
  Placement = pos=(6.45,5.625,1.2) rot=(0,0,1;0rad)
  shape: bbox 2.1 x 1.35 x 0.6 mm, 52 faces, 3 solids (baked)
FEATURE [Part::Feature] Part__Feature031  label="RESC-0808"
  Placement = pos=(6.45,3.085,1.2) rot=(0,0,1;0rad)
  shape: bbox 2.1 x 1.35 x 0.6 mm, 52 faces, 3 solids (baked)
FEATURE [Part::Feature] Part__Feature032  label="RESC-0809"
  Placement = pos=(6.45,0.545,1.2) rot=(0,0,1;0rad)
  shape: bbox 2.1 x 1.35 x 0.6 mm, 52 faces, 3 solids (baked)
FEATURE [Part::Feature] Part__Feature033  label="CAPC-0805-T0.95-BN"
  Placement = pos=(6.45,-1.995,1.2) rot=(0,0,1;0rad)
  shape: bbox 2.1 x 1.35 x 0.95 mm, 34 faces (baked)
FEATURE [Part::Feature] Part__Feature034  label="CAPC-0805-T0.95-BN001"
  Placement = pos=(6.45,-4.535,1.2) rot=(0,0,1;0rad)
  shape: bbox 2.1 x 1.35 x 0.95 mm, 34 faces (baked)
FEATURE [App::Part] IR_Sensor_FC_51  label="IR_Sensor_FC-052"
  Group = -> [Part__Feature016,Part__Feature017,Part__Feature018,Part__Feature019,LED_5mm,LED_5mm_foto,Part__Feature024,Part__Feature025,Part__Feature026,Part__Feature027,Part__Feature028,Part__Feature029,Part__Feature030,Part__Feature031,Part__Feature032,Part__Feature033,Part__Feature034]
  Origin = -> Origin003
  Placement = pos=(80,-30,1) rot=(0,1,0;1.5708rad)
FEATURE [Part::Feature] Part__Feature035  label="3362P-1-102LF001"
  Placement = pos=(0.5,-3.2,1.53) rot=(1,0,0;1.5708rad)
  shape: bbox 6.672 x 6.672 x 7.467 mm, 233 faces, 2 solids (baked)
FEATURE [Part::Feature] Part__Feature036  label="IR_Sensor_FC-054"
  shape: bbox 31 x 14 x 1.25 mm, 435 faces (baked)
FEATURE [Part::Feature] Part__Feature037  label="KPTR-3216CGCK002"
  Placement = pos=(-8.7,3.8,1.45) rot=(1,0,0;3.14159rad)
  shape: bbox 3.203 x 1.603 x 1.053 mm, 75 faces, 4 solids (baked)
FEATURE [Part::Feature] Part__Feature038  label="KPTR-3216CGCK003"
  Placement = pos=(-8.7,-3.8,1.45) rot=(1,0,0;3.14159rad)
  shape: bbox 3.203 x 1.603 x 1.053 mm, 75 faces, 4 solids (baked)
FEATURE [Part::Feature] Part__Feature039  label="COMPOUND004"
  shape: bbox 5.5 x 6.7 x 11.78 mm, 50 faces, 3 solids (baked)
FEATURE [Part::Feature] Part__Feature040  label="COMPOUND005"
  shape: bbox 3.2 x 2 x 0.48 mm, 0 faces, 0 solids (baked)
FEATURE [App::Part] LED_5mm001  label="LED 5mm001"
  Group = -> [Part__Feature039,Part__Feature040]
  Origin = -> Origin004
  Placement = pos=(15.74,3.64,3) rot=(0.57735,0.57735,0.57735;2.0944rad)
FEATURE [Part::Feature] Part__Feature041  label="COMPOUND006"
  shape: bbox 5.5 x 6.7 x 11.78 mm, 50 faces, 3 solids (baked)
FEATURE [Part::Feature] Part__Feature042  label="COMPOUND007"
  shape: bbox 3.2 x 2 x 0.48 mm, 0 faces, 0 solids (baked)
FEATURE [App::Part] LED_5mm_foto001  label="LED 5mm_foto001"
  Group = -> [Part__Feature041,Part__Feature042]
  Origin = -> Origin005
  Placement = pos=(15.74,-3.64,3) rot=(0.57735,0.57735,0.57735;2.0944rad)
FEATURE [Part::Feature] Part__Feature043  label="RESC-0810"
  Placement = pos=(-4.525,-3.15,1.2) rot=(0,0,-1;1.5708rad)
  shape: bbox 1.35 x 2.1 x 0.6 mm, 52 faces, 3 solids (baked)
FEATURE [Part::Feature] Part__Feature044  label="RESC-0811"
  Placement = pos=(-4.525,3.25,1.2) rot=(0,0,1;1.5708rad)
  shape: bbox 1.35 x 2.1 x 0.6 mm, 52 faces, 3 solids (baked)
FEATURE [Part::Feature] Part__Feature045  label="SOIC8-150-051"
  Placement = pos=(0.55,3.85,1.2) rot=(1,0,0;1.5708rad)
  shape: bbox 6 x 4.9 x 1.91 mm, 105 faces (baked)
FEATURE [Part::Feature] Part__Feature046  label="1 Pin 2.54 mm Right Angle Single Row Pin Header Male 90 degrees Needl
e Connector003"
  Placement = pos=(-13.5,2.54,-1.76) rot=(0,0,1;3.14159rad)
  shape: bbox 8.45 x 2.54 x 7.3 mm, 40 faces, 2 solids (baked)
FEATURE [Part::Feature] Part__Feature047  label="1 Pin 2.54 mm Right Angle Single Row Pin Header Male 90 degrees Needl
e Connector004"
  Placement = pos=(-13.5,2e-15,-1.76) rot=(0,0,1;3.14159rad)
  shape: bbox 8.45 x 2.54 x 7.3 mm, 40 faces, 2 solids (baked)
FEATURE [Part::Feature] Part__Feature048  label="1 Pin 2.54 mm Right Angle Single Row Pin Header Male 90 degrees Needl
e Connector005"
  Placement = pos=(-13.5,-2.54,-1.76) rot=(0,0,1;3.14159rad)
  shape: bbox 8.45 x 2.54 x 7.3 mm, 40 faces, 2 solids (baked)
FEATURE [Part::Feature] Part__Feature049  label="RESC-0812"
  Placement = pos=(6.45,5.625,1.2) rot=(0,0,1;0rad)
  shape: bbox 2.1 x 1.35 x 0.6 mm, 52 faces, 3 solids (baked)
FEATURE [Part::Feature] Part__Feature050  label="RESC-0813"
  Placement = pos=(6.45,3.085,1.2) rot=(0,0,1;0rad)
  shape: bbox 2.1 x 1.35 x 0.6 mm, 52 faces, 3 solids (baked)
FEATURE [Part::Feature] Part__Feature051  label="RESC-0814"
  Placement = pos=(6.45,0.545,1.2) rot=(0,0,1;0rad)
  shape: bbox 2.1 x 1.35 x 0.6 mm, 52 faces, 3 solids (baked)
FEATURE [Part::Feature] Part__Feature052  label="CAPC-0805-T0.95-BN002"
  Placement = pos=(6.45,-1.995,1.2) rot=(0,0,1;0rad)
  shape: bbox 2.1 x 1.35 x 0.95 mm, 34 faces (baked)
FEATURE [Part::Feature] Part__Feature053  label="CAPC-0805-T0.95-BN003"
  Placement = pos=(6.45,-4.535,1.2) rot=(0,0,1;0rad)
  shape: bbox 2.1 x 1.35 x 0.95 mm, 34 faces (baked)
FEATURE [App::Part] IR_Sensor_FC_052  label="IR_Sensor_FC-053"
  Group = -> [Part__Feature035,Part__Feature036,Part__Feature037,Part__Feature038,LED_5mm001,LED_5mm_foto001,Part__Feature043,Part__Feature044,Part__Feature045,Part__Feature046,Part__Feature047,Part__Feature048,Part__Feature049,Part__Feature050,Part__Feature051,Part__Feature052,Part__Feature053]
  Origin = -> Origin006
  Placement = pos=(80,30,1) rot=(0,1,0;1.5708rad)
FEATURE [Part::Feature] Part__Feature054  label="Buzzer_3V"
  Placement = pos=(-7,-47,63) rot=(0,0,1;3.14159rad)
  shape: bbox 15.45 x 14.15 x 12 mm, 409 faces (baked)
FEATURE [Part::Torus] Torus  label="Cubierta"
  Angle1 = -180
  Angle2 = 180
  Angle3 = 360
  AttacherType = Attacher::AttachEngine3D
  Placement = pos=(-2,-76,0) rot=(1,0,0;1.5708rad)
  Radius1 = 37.5
  Radius2 = 2
FEATURE [Part::Torus] Torus001  label="Cubierta001"
  Angle1 = -180
  Angle2 = 180
  Angle3 = 360
  AttacherType = Attacher::AttachEngine3D
  Placement = pos=(-2,79,0) rot=(1,0,0;1.5708rad)
  Radius1 = 37.5
  Radius2 = 2
FEATURE [Mesh::Feature] ballCaster
FEATURE [Part::Box] Box031  label="Pista"
  AttacherType = Attacher::AttachEngine3D
  Height = 3
  Length = 2000
  Placement = pos=(-500,0,-40) rot=(0,0,1;0rad)
  Width = 29
